annotation { "Feature Type Name" : "Feature", "Feature Type Description" : "" }
export const myFeature = defineFeature(function(context is Context, id is Id, definition is map)
    precondition{}
    {
        {
            var Q0;
            Q0=qCreatedBy(makeId("Top.planeOp"),FACE);
            var sketch = newSketch(context, id + "F0", { "sketchPlane" : qUnion([Q0])});
            skLineSegment(sketch, "E0", {"start": v(-57.34, -23.28) * mm, "end": v(-57.34, -13.16) * mm});
            skLineSegment(sketch, "E1", {"start": v(-57.34, 27.6) * mm, "end": v(39.18, 27.6) * mm});
            skLineSegment(sketch, "E2", {"start": v(41.72, 25.06) * mm, "end": v(41.72, 10.4) * mm});
            skLineSegment(sketch, "E3", {"start": v(41.72, 10.4) * mm, "end": v(41.72, 10.4) * mm});
            skLineSegment(sketch, "E4", {"start": v(44.26, 7.86) * mm, "end": v(44.26, -13.29) * mm});
            skLineSegment(sketch, "E5", {"start": v(41.72, -15.83) * mm, "end": v(41.72, -15.83) * mm});
            skLineSegment(sketch, "E6", {"start": v(41.72, -15.83) * mm, "end": v(41.72, -23.28) * mm});
            skLineSegment(sketch, "E7", {"start": v(41.72, -23.28) * mm, "end": v(-57.34, -23.28) * mm});
            skLineSegment(sketch, "E8.bottom", {"start": v(-65.3, 24.72) * mm, "end": v(-46.65, 24.72) * mm});
            skLineSegment(sketch, "E8.top", {"start": v(-65.3, 12.19) * mm, "end": v(-46.65, 12.19) * mm});
            skLineSegment(sketch, "E8.left", {"start": v(-65.3, 24.72) * mm, "end": v(-65.3, 12.19) * mm});
            skLineSegment(sketch, "E8.right", {"start": v(-46.65, 24.72) * mm, "end": v(-46.65, 12.19) * mm});
            skLineSegment(sketch, "E9.bottom", {"start": v(-64.13, -2.38) * mm, "end": v(-46.65, -2.38) * mm});
            skLineSegment(sketch, "E9.top", {"start": v(-64.13, -13.16) * mm, "end": v(-46.65, -13.16) * mm});
            skLineSegment(sketch, "E9.left", {"start": v(-64.13, -2.38) * mm, "end": v(-64.13, -13.16) * mm});
            skLineSegment(sketch, "E9.right", {"start": v(-46.65, -2.38) * mm, "end": v(-46.65, -13.16) * mm});
            skLineSegment(sketch, "E10.trimOffspring", {"start": v(-57.34, 24.72) * mm, "end": v(-57.34, 27.6) * mm});
            skLineSegment(sketch, "E11.trimOffspring", {"start": v(-57.34, -2.38) * mm, "end": v(-57.34, 12.19) * mm});
            skPoint(sketch, "E12.visualSharp", {"position": v(41.72, 27.6) * mm});
            skArc(sketch, "E12.filletArc", {"start": v(41.72, 25.06) * mm, "mid": v(40.97, 26.86) * mm, "end": v(39.18, 27.6) * mm});
            skPoint(sketch, "E13.visualSharp", {"position": v(44.26, -15.83) * mm});
            skArc(sketch, "E13.filletArc", {"start": v(41.72, -15.83) * mm, "mid": v(43.51, -15.08) * mm, "end": v(44.26, -13.29) * mm});
            skPoint(sketch, "E14.visualSharp", {"position": v(44.26, 10.4) * mm});
            skArc(sketch, "E14.filletArc", {"start": v(44.26, 7.86) * mm, "mid": v(43.51, 9.65) * mm, "end": v(41.72, 10.4) * mm});
            skText(sketch, "E15", { "text": "Arduino Mega", "fontName": "OpenSans-Bold.ttf"});
            const initialGuessF0  = {"E15": [-0.0306, -0.0042, 1, 0, 0.0062]};
            skSetInitialGuess(sketch, initialGuessF0);
            skSolve(sketch);
        }
        {
            var Q0;
            {var subQ4=sQuery(id+"F0.wireOp",EDGE,"E0");Q0=makeQuery(id+"F0.imprint","IMPRINT",FACE,{"disambiguationData":[TD([[makeQuery(id+"F0.imprint","IMPRINT",EDGE,{"derivedFrom":subQ4}),-1.0]])]});}
            extrude(context, id + "F1", {"entities" : qUnion([Q0]), "depth" : 1 * mm, "offsetDistance" : 25 * mm});
        }
        {
            var Q0;
            {var subQ3=sQuery(id+"F0.wireOp",EDGE,"E8.left");Q0=makeQuery(id+"F0.imprint","IMPRINT",FACE,{"disambiguationData":[TD([[makeQuery(id+"F0.imprint","IMPRINT",EDGE,{"derivedFrom":subQ3}),1.0]])]});}
            var Q1;
            {var subQ3=sQuery(id+"F0.wireOp",EDGE,"E9.left");Q1=makeQuery(id+"F0.imprint","IMPRINT",FACE,{"disambiguationData":[TD([[makeQuery(id+"F0.imprint","IMPRINT",EDGE,{"derivedFrom":subQ3}),1.0]])]});}
            extrude(context, id + "F2", {"entities" : qUnion([Q0, Q1]), "endBound" : BoundingType.SYMMETRIC, "depth" : 10 * mm, "offsetDistance" : 25 * mm});
        }
    });